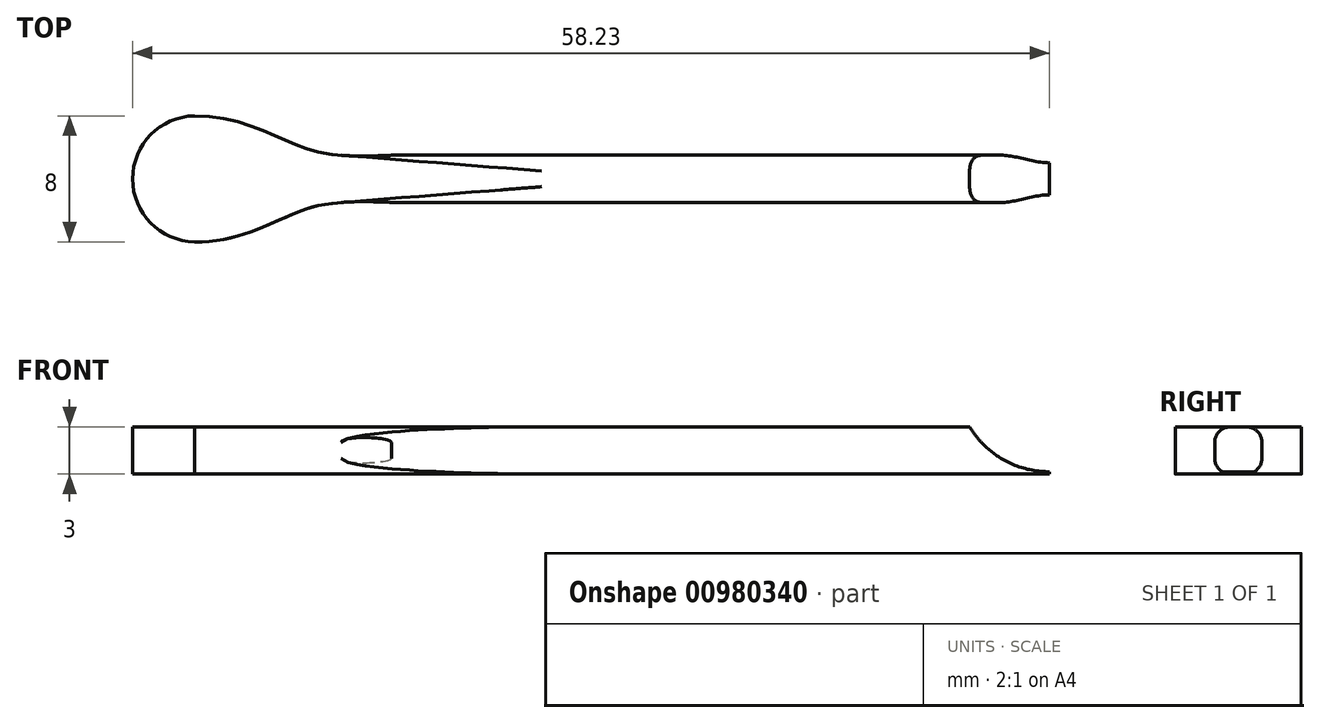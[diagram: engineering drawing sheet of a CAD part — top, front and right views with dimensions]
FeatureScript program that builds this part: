
annotation { "Feature Type Name" : "Feature", "Feature Type Description" : "" }
export const myFeature = defineFeature(function(context is Context, id is Id, definition is map)
    precondition{}
    {
        {
            var Q0;
            Q0=qCreatedBy(makeId("Top.planeOp"),FACE);
            var sketch = newSketch(context, id + "F0", { "sketchPlane" : qUnion([Q0])});
            skLineSegment(sketch, "E0.bottom", {"start": v(0, 0) * mm, "end": v(-40, 0) * mm});
            skLineSegment(sketch, "E0.top", {"start": v(0, 3) * mm, "end": v(-40, 3) * mm});
            skLineSegment(sketch, "E0.left", {"start": v(0, 0) * mm, "end": v(0, 3) * mm});
            skArc(sketch, "E1", {"start": v(-49.3, 5.5) * mm, "mid": v(-53.23, 1.5) * mm, "end": v(-49.3, -2.5) * mm});
            skPoint(sketch, "E2.orphan", {"position": v(-49.23, 3) * mm});
            skPoint(sketch, "E3.orphan", {"position": v(-49.23, 0) * mm});
            skFitSpline(sketch, "E4", {"points": [v(-49.3, 5.5) * mm, v(-43.9, 4.12) * mm, v(-36.79, 3) * mm], "startDerivative": vector(13.11, 0.37) * mm, "endDerivative": vector(24.69, 1.32) * mm});
            skLineSegment(sketch, "E5", {"start": v(0, 1.5) * mm, "end": v(-32.45, 1.5) * mm, "construction": true});
            skFitSpline(sketch, "E6.MirrorCS", {"points": [v(-49.3, -2.5) * mm, v(-43.9, -1.12) * mm, v(-36.79, 0) * mm], "startDerivative": vector(13.11, -0.37) * mm, "endDerivative": vector(24.69, -1.32) * mm});
            skSolve(sketch);
        }
        {
            var Q0;
            {var subQ0=sQuery(id+"F0.wireOp",EDGE,"E0.left");Q0=makeQuery(id+"F0.imprint","IMPRINT",FACE,{"disambiguationData":[TD([[makeQuery(id+"F0.imprint","IMPRINT",EDGE,{"derivedFrom":subQ0}),1.0]])]});}
            extrude(context, id + "F1", {"entities" : qUnion([Q0]), "depth" : 3 * mm, "offsetDistance" : 25 * mm});
        }
        {
            var Q0;
            Q0=makeQuery(id+"F1.opExtrude","CAP_EDGE",EDGE,{"disambiguationData":[OSD([sQuery(id+"F0.wireOp",EDGE,"E0.bottom")])],"isStart":false});
            var Q1;
            Q1=makeQuery(id+"F1.opExtrude","CAP_EDGE",EDGE,{"disambiguationData":[OSD([sQuery(id+"F0.wireOp",EDGE,"E0.top")])],"isStart":false});
            var Q2;
            Q2=makeQuery(id+"F1.opExtrude","CAP_EDGE",EDGE,{"disambiguationData":[OSD([sQuery(id+"F0.wireOp",EDGE,"E0.bottom")])],"isStart":true});
            var Q3;
            Q3=makeQuery(id+"F1.opExtrude","CAP_EDGE",EDGE,{"disambiguationData":[OSD([sQuery(id+"F0.wireOp",EDGE,"E0.top")])],"isStart":true});
            fillet(context, id + "F2", {"entities" : qUnion([Q0, Q1, Q2, Q3]), "radius" : 1 * mm, "tangentPropagation" : true, "allowEdgeOverflow" : false});
        }
        {
            var Q0;
            Q0=makeQuery(id+"F1.opExtrude","SWEPT_FACE",FACE,{"disambiguationData":[OSD([sQuery(id+"F0.wireOp",EDGE,"E0.left")])]});
            extrude(context, id + "F3", {"entities" : qUnion([Q0]), "operationType" : NewBodyOperationType.ADD, "depth" : 5 * mm, "offsetDistance" : 25 * mm});
        }
        {
            var Q0;
            {var subQ0=sQuery(id+"F0.wireOp",EDGE,"E0.left");var subQ1=sQuery(id+"F0.wireOp",EDGE,"E0.top");Q0=makeQuery(id+"F3.boolean.opBoolean","MERGE",FACE,{"derivedFrom":[makeQuery(id+"F1.opExtrude","SWEPT_FACE",FACE,{"disambiguationData":[OSD([subQ1])]}),makeQuery(id+"F3.opExtrude","SWEPT_FACE",FACE,{"disambiguationData":[OSD([subQ1,subQ0]),TDD([makeQuery(id+"F1.opExtrude","SWEPT_EDGE",EDGE,{"disambiguationData":[OSD([subQ1,subQ0])]})])]})]});}
            var sketch = newSketch(context, id + "F4", { "sketchPlane" : qUnion([Q0])});
            skCircle(sketch, "E7", {"center": v(-4.98, 6.04) * mm, "radius": 5.9 * mm});
            skSolve(sketch);
        }
        {
            var Q0;
            {var subQ1=sQuery(id+"F0.wireOp",EDGE,"E0.left");var subQ3=sQuery(id+"F0.wireOp",EDGE,"E0.top");var subQ11=makeQuery(id+"F3.opExtrude","CAP_EDGE",EDGE,{"disambiguationData":[OSD([subQ3,subQ1]),TDD([makeQuery(id+"F1.opExtrude","SWEPT_EDGE",EDGE,{"disambiguationData":[OSD([subQ3,subQ1])]})])],"isStart":false});Q0=makeQuery(id+"F4.imprint","IMPRINT",FACE,{"disambiguationData":[TD([[makeQuery(id+"F4.imprint","IMPRINT",EDGE,{"derivedFrom":subQ11}),-1.0]])]});}
            var Q1;
            {var subQ1=sQuery(id+"F0.wireOp",EDGE,"E0.left");var subQ3=sQuery(id+"F0.wireOp",EDGE,"E0.top");var subQ11=makeQuery(id+"F3.opExtrude","CAP_EDGE",EDGE,{"disambiguationData":[OSD([subQ3,subQ1]),TDD([makeQuery(id+"F1.opExtrude","SWEPT_EDGE",EDGE,{"disambiguationData":[OSD([subQ3,subQ1])]})])],"isStart":false});Q1=makeQuery(id+"F4.imprint","IMPRINT",FACE,{"disambiguationData":[TD([[makeQuery(id+"F4.imprint","IMPRINT",EDGE,{"derivedFrom":subQ11}),1.0]])]});}
            extrude(context, id + "F5", {"entities" : qUnion([Q0, Q1]), "operationType" : NewBodyOperationType.REMOVE, "oppositeDirection" : true, "depth" : 10 * mm, "offsetDistance" : 25 * mm});
        }
    });
